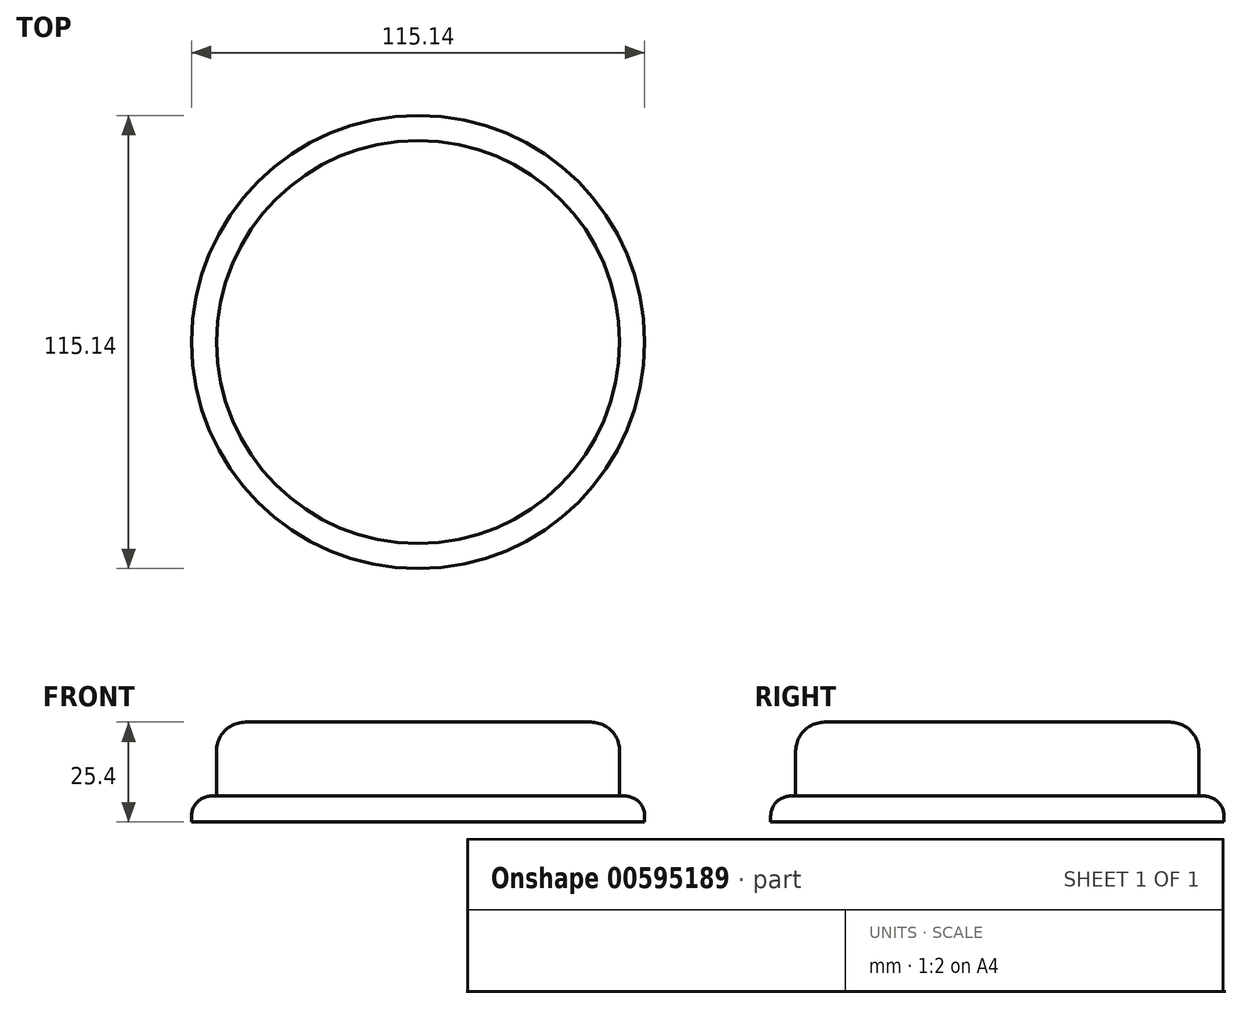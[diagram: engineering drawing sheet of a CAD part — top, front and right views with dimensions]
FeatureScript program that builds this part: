
annotation { "Feature Type Name" : "Feature", "Feature Type Description" : "" }
export const myFeature = defineFeature(function(context is Context, id is Id, definition is map)
    precondition{}
    {
        {
            var Q0;
            Q0=qCreatedBy(makeId("Top.planeOp"),FACE);
            var sketch = newSketch(context, id + "F0", { "sketchPlane" : qUnion([Q0])});
            skCircle(sketch, "E0", {"center": v(0, 0) * mm, "radius": 51.22 * mm});
            skCircle(sketch, "E1.0", {"center": v(0, 0) * mm, "radius": 57.57 * mm});
            skSolve(sketch);
        }
        {
            var Q0;
            Q0=sQuery(id+"F0.wireOp",EDGE,"E0");
            extrude(context, id + "F1", {"bodyType" : ToolBodyType.SURFACE, "surfaceEntities" : qUnion([Q0]), "endBound" : BoundingType.SYMMETRIC, "depth" : 5.08 * mm, "offsetDistance" : 25.4 * mm});
        }
        {
            var Q0;
            Q0=makeQuery(id+"F0.imprint","IMPRINT",FACE,{"disambiguationData":[TD([[makeQuery(id+"F0.imprint","IMPRINT",EDGE,{"derivedFrom":sQuery(id+"F0.wireOp",EDGE,"E0")}),1.0]])]});
            extrude(context, id + "F2", {"entities" : qUnion([Q0]), "depth" : 25.4 * mm, "offsetDistance" : 25.4 * mm});
        }
        {
            var Q0;
            Q0=makeQuery(id+"F2.opExtrude","CAP_EDGE",EDGE,{"disambiguationData":[OSD([sQuery(id+"F0.wireOp",EDGE,"E0")])],"isStart":false});
            fillet(context, id + "F3", {"entities" : qUnion([Q0]), "radius" : 7.36 * mm, "tangentPropagation" : true, "allowEdgeOverflow" : false});
        }
        {
            var Q0;
            Q0=makeQuery(id+"F0.imprint","IMPRINT",FACE,{"disambiguationData":[TD([[makeQuery(id+"F0.imprint","IMPRINT",EDGE,{"derivedFrom":sQuery(id+"F0.wireOp",EDGE,"E0")}),-1.0]])]});
            extrude(context, id + "F4", {"entities" : qUnion([Q0]), "operationType" : NewBodyOperationType.ADD, "depth" : 6.6 * mm, "offsetDistance" : 25.4 * mm});
        }
        {
            var Q0;
            Q0=makeQuery(id+"F4.opExtrude","CAP_EDGE",EDGE,{"disambiguationData":[OSD([sQuery(id+"F0.wireOp",EDGE,"E1.0")])],"isStart":false});
            fillet(context, id + "F5", {"entities" : qUnion([Q0]), "radius" : 5.08 * mm, "tangentPropagation" : true, "allowEdgeOverflow" : false});
        }
    });
